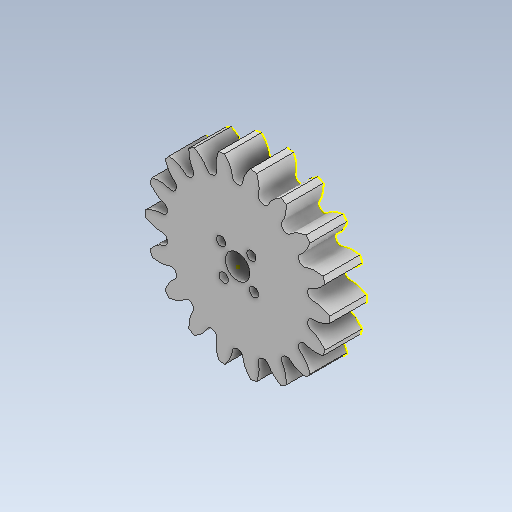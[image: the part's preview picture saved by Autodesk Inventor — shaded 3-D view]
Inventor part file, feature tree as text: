
AUTODESK INVENTOR PART (.ipt)
format: ipt  version: 2021 (Build 250183000, 183)  size: 421,376 bytes
history: native  units: in
note: dims shown in document units (in); Inventor stores cm internally (conversion verified against a paired STEP export)
features: sketch x3, extrude x3, projected_geometry x1
ambient origin geometry x8: Origin, YZ Plane, XZ Plane, XY Plane, X Axis, Y Axis, Z Axis, Center Point
bodies: Solid2 (feature_tree), Solid1 (feature_tree)
feature tree (7):
  sketch  "Sketch1"  dims[d0=0.3937in d1=0.0in d2=0.4724in d3=0.0in]
  extrude  "Extrusion1"  Depth=0.4724in TaperAngle=0.0deg
  extrude  "Extrusion2"  Depth=0.1181in
  extrude  "Extrusion3"  Depth=0.1181in
  sketch  "Sketch4"  dims[d8=0.2756in d9=0.1181in d10=0.2756in d11=0.1181in d12=0.2756in d13=0.0in d14=0.0in d26=0.0197in d27=1.9685in d28=0.0197in d29=1.9685in]
  projected_geometry  "Projected Loop1"
  sketch  "Sketch2"  dims[d4=0.315in d7=0.1181in]
